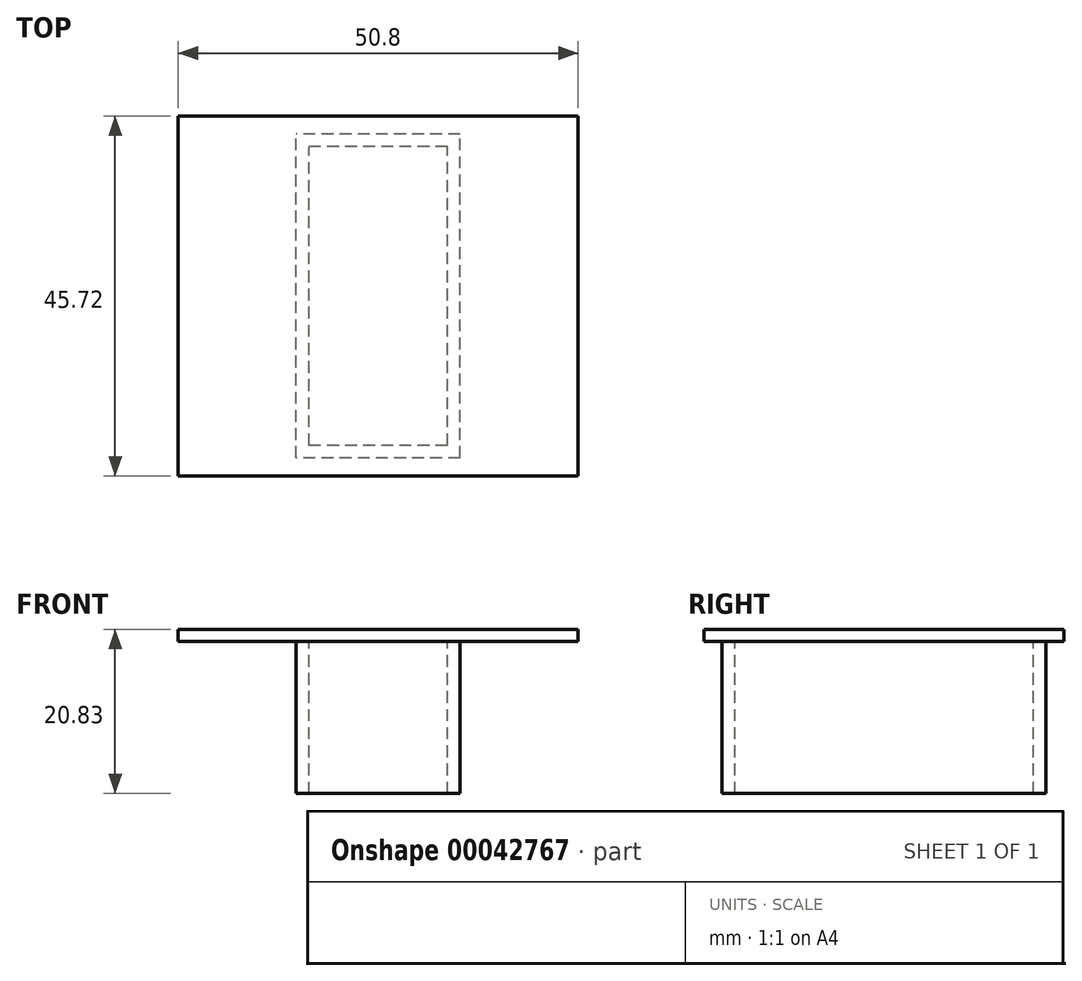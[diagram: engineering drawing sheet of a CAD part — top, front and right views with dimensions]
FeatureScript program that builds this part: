
annotation { "Feature Type Name" : "Feature", "Feature Type Description" : "" }
export const myFeature = defineFeature(function(context is Context, id is Id, definition is map)
    precondition{}
    {
        {
            var Q0;
            Q0=qCreatedBy(makeId("Top.planeOp"),FACE);
            var sketch = newSketch(context, id + "F0", { "sketchPlane" : qUnion([Q0])});
            skLineSegment(sketch, "E0.rect.bottom", {"start": v(25.4, 22.86) * mm, "end": v(-25.4, 22.86) * mm});
            skLineSegment(sketch, "E0.rect.top", {"start": v(25.4, -22.86) * mm, "end": v(-25.4, -22.86) * mm});
            skLineSegment(sketch, "E0.rect.left", {"start": v(25.4, 22.86) * mm, "end": v(25.4, -22.86) * mm});
            skLineSegment(sketch, "E0.rect.right", {"start": v(-25.4, 22.86) * mm, "end": v(-25.4, -22.86) * mm});
            skPoint(sketch, "E0.rect.middle", {"position": v(0, 0) * mm});
            skSolve(sketch);
        }
        {
            var Q0;
            Q0=makeQuery(id+"F0.imprint","IMPRINT",FACE,{"disambiguationData":[TD([[makeQuery(id+"F0.imprint","IMPRINT",EDGE,{"derivedFrom":sQuery(id+"F0.wireOp",EDGE,"E0.rect.bottom")}),1.0]])]});
            extrude(context, id + "F1", {"entities" : qUnion([Q0]), "oppositeDirection" : true, "depth" : 1.51 * mm});
        }
        {
            var Q0;
            Q0=makeQuery(id+"F1.opExtrude","CAP_FACE",FACE,{"disambiguationData":[OSD([sQuery(id+"F0.wireOp",EDGE,"E0.rect.bottom"),sQuery(id+"F0.wireOp",EDGE,"E0.rect.top"),sQuery(id+"F0.wireOp",EDGE,"E0.rect.left"),sQuery(id+"F0.wireOp",EDGE,"E0.rect.right")])],"isStart":false});
            var sketch = newSketch(context, id + "F2", { "sketchPlane" : qUnion([Q0])});
            skLineSegment(sketch, "E1.rect.bottom", {"start": v(10.41, 20.57) * mm, "end": v(-10.41, 20.57) * mm});
            skLineSegment(sketch, "E1.rect.top", {"start": v(10.41, -20.57) * mm, "end": v(-10.41, -20.57) * mm});
            skLineSegment(sketch, "E1.rect.left", {"start": v(10.41, 20.57) * mm, "end": v(10.41, -20.57) * mm});
            skLineSegment(sketch, "E1.rect.right", {"start": v(-10.41, 20.57) * mm, "end": v(-10.41, -20.57) * mm});
            skPoint(sketch, "E1.rect.middle", {"position": v(0, 0) * mm});
            skLineSegment(sketch, "E2.rect.bottom", {"start": v(8.8, 18.97) * mm, "end": v(-8.8, 18.97) * mm});
            skLineSegment(sketch, "E2.rect.top", {"start": v(8.8, -18.97) * mm, "end": v(-8.8, -18.97) * mm});
            skLineSegment(sketch, "E2.rect.left", {"start": v(8.8, 18.97) * mm, "end": v(8.8, -18.97) * mm});
            skLineSegment(sketch, "E2.rect.right", {"start": v(-8.8, 18.97) * mm, "end": v(-8.8, -18.97) * mm});
            skSolve(sketch);
        }
        {
            var Q0;
            Q0=makeQuery(id+"F2.imprint","IMPRINT",FACE,{"disambiguationData":[TD([[makeQuery(id+"F2.imprint","IMPRINT",EDGE,{"derivedFrom":sQuery(id+"F2.wireOp",EDGE,"E1.rect.bottom")}),1.0]])]});
            extrude(context, id + "F3", {"entities" : qUnion([Q0]), "operationType" : NewBodyOperationType.ADD, "depth" : 19.32 * mm});
        }
    });
